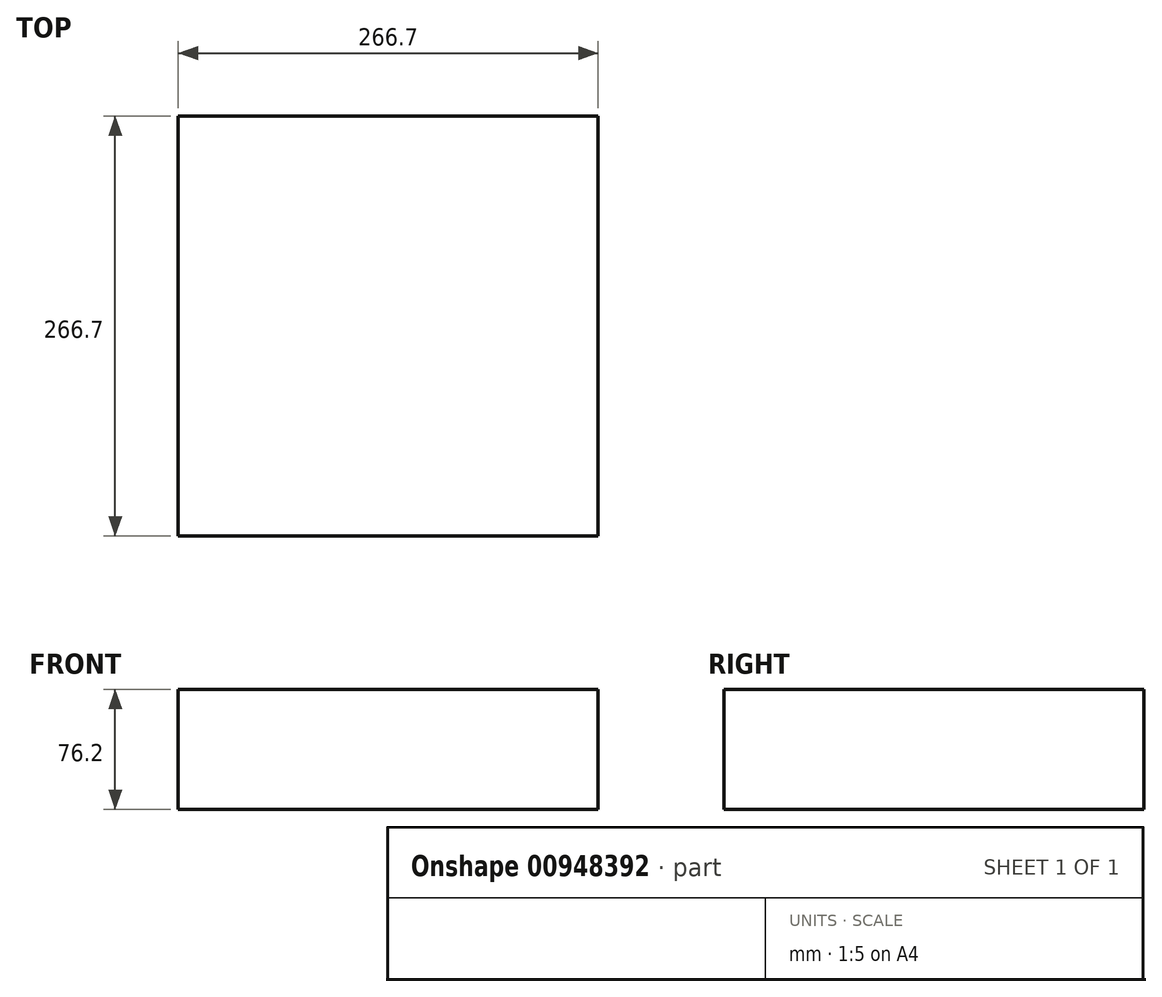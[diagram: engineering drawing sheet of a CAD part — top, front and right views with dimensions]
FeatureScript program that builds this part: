
annotation { "Feature Type Name" : "Feature", "Feature Type Description" : "" }
export const myFeature = defineFeature(function(context is Context, id is Id, definition is map)
    precondition{}
    {
        {
            var Q0;
            Q0=qCreatedBy(makeId("Top.planeOp"),FACE);
            var sketch = newSketch(context, id + "F0", { "sketchPlane" : qUnion([Q0])});
            skLineSegment(sketch, "E0.bottom", {"start": v(133.35, 133.35) * mm, "end": v(-133.35, 133.35) * mm});
            skLineSegment(sketch, "E0.top", {"start": v(133.35, -133.35) * mm, "end": v(-133.35, -133.35) * mm});
            skLineSegment(sketch, "E0.left", {"start": v(133.35, 133.35) * mm, "end": v(133.35, -133.35) * mm});
            skLineSegment(sketch, "E0.right", {"start": v(-133.35, 133.35) * mm, "end": v(-133.35, -133.35) * mm});
            skPoint(sketch, "E0.middle", {"position": v(0, 0) * mm});
            skSolve(sketch);
        }
        {
            var Q0;
            Q0=makeQuery(id+"F0.imprint","IMPRINT",FACE,{"disambiguationData":[TD([[makeQuery(id+"F0.imprint","IMPRINT",EDGE,{"derivedFrom":sQuery(id+"F0.wireOp",EDGE,"E0.bottom")}),1.0]])]});
            extrude(context, id + "F1", {"entities" : qUnion([Q0]), "depth" : 76.2 * mm, "offsetDistance" : 25.4 * mm});
        }
    });
